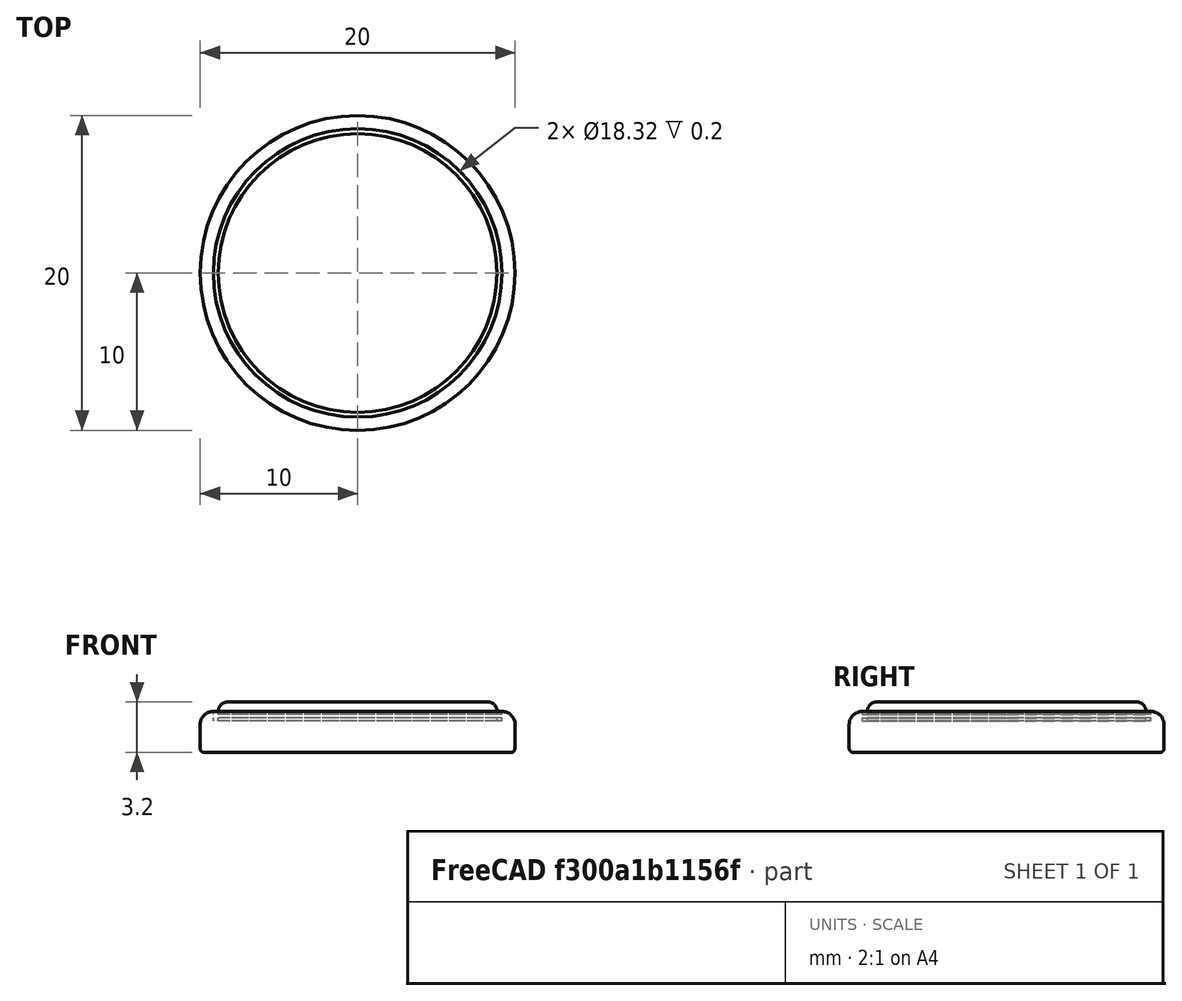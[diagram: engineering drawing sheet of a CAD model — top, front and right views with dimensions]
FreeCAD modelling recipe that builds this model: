
FCSTD DOCUMENT  (FreeCAD 0.14R3702 (Git))
Label: CR2032
License: CC-BY 3.0
LicenseURL: http://creativecommons.org/licenses/by/3.0/
objects: Part::Cylinder×4, Part::MultiFuse×2, Part::Cut×1, Part::Fillet×1
note: 8 computed .brp shape members not serialized (recipe doc carries the construction recipe); baked Part::Feature solids carry a one-line shape summary decoded from their .brp

FEATURE [Part::Cylinder] Cylinder  label="battery_main"
  Angle = 360
  Height = 2.6
  Radius = 10
FEATURE [Part::Cylinder] Cylinder001  label="battery_minus"
  Angle = 360
  Height = 3
  Placement = pos=(0,0,0.2) rot=(0,0,1;0rad)
  Radius = 8.85
FEATURE [Part::Cylinder] Cylinder002  label="inside_cut"
  Angle = 360
  Height = 18
  Placement = pos=(0,0,2) rot=(0,0,1;0rad)
  Radius = 9.16
FEATURE [Part::Cut] Cut
  Base = -> Cylinder
  Tool = -> Cylinder002
FEATURE [Part::MultiFuse] Fusion
  Shapes = -> [Cylinder001,Cut]
FEATURE [Part::Fillet] Fillet  label="battery"
  Base = -> Fusion
  Edges = 3 edges: [Edge1 r=0.6,Edge7 r=0.83,Edge9 r=0.25]
FEATURE [Part::Cylinder] Cylinder003  label="black_ring"
  Angle = 360
  Height = 0.2
  Placement = pos=(0,0,2.2) rot=(0,0,1;0rad)
  Radius = 9.16
FEATURE [Part::MultiFuse] Fusion001  label="battery_final"
  Shapes = -> [Cylinder003,Fillet]
